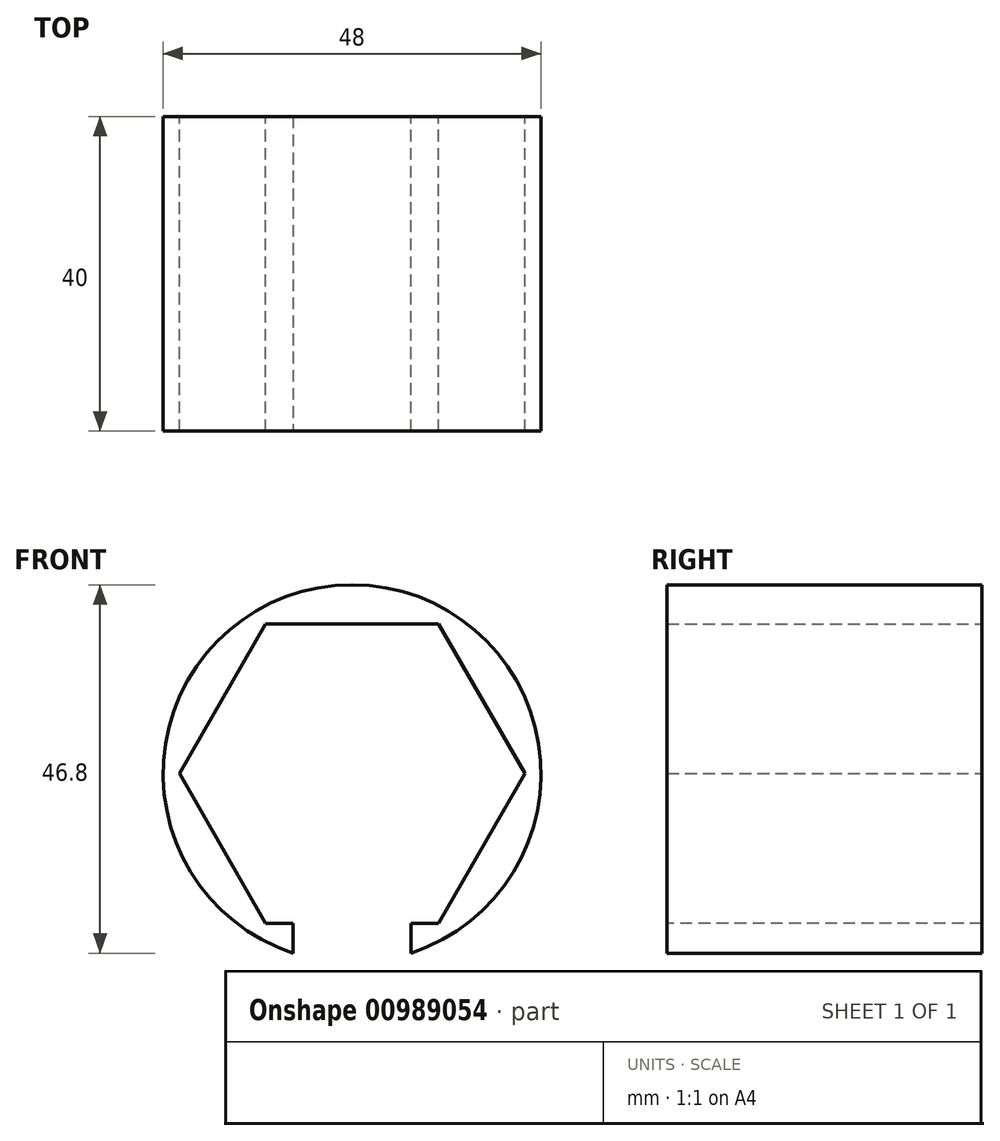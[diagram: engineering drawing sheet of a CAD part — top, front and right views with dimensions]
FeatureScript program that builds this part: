
annotation { "Feature Type Name" : "Feature", "Feature Type Description" : "" }
export const myFeature = defineFeature(function(context is Context, id is Id, definition is map)
    precondition{}
    {
        {
            var Q0;
            Q0=qCreatedBy(makeId("Front.planeOp"),FACE);
            var sketch = newSketch(context, id + "F0", { "sketchPlane" : qUnion([Q0])});
            skCircle(sketch, "E0.cCircle", {"center": v(0, 0) * mm, "radius": 19 * mm, "construction": true});
            skLineSegment(sketch, "E0.0", {"start": v(10.97, 19) * mm, "end": v(21.94, 0) * mm});
            skLineSegment(sketch, "E0.1", {"start": v(21.94, 0) * mm, "end": v(10.97, -19) * mm});
            skLineSegment(sketch, "E0.2", {"start": v(10.97, -19) * mm, "end": v(-10.97, -19) * mm});
            skLineSegment(sketch, "E0.3", {"start": v(-10.97, -19) * mm, "end": v(-21.94, 0) * mm});
            skLineSegment(sketch, "E0.4", {"start": v(-21.94, 0) * mm, "end": v(-10.97, 19) * mm});
            skLineSegment(sketch, "E0.5", {"start": v(-10.97, 19) * mm, "end": v(10.97, 19) * mm});
            skPoint(sketch, "E0.0.midPoint", {"position": v(16.45, 9.5) * mm});
            skCircle(sketch, "E1", {"center": v(0, 0) * mm, "radius": 24 * mm});
            skSolve(sketch);
        }
        {
            var Q0;
            Q0=makeQuery(id+"F0.imprint","IMPRINT",FACE,{"disambiguationData":[TD([[makeQuery(id+"F0.imprint","IMPRINT",EDGE,{"derivedFrom":sQuery(id+"F0.wireOp",EDGE,"E0.0")}),1.0]])]});
            extrude(context, id + "F1", {"entities" : qUnion([Q0]), "depth" : 40 * mm, "offsetDistance" : 25 * mm});
        }
        {
            var Q0;
            Q0=qCreatedBy(makeId("Top.planeOp"),FACE);
            var sketch = newSketch(context, id + "F2", { "sketchPlane" : qUnion([Q0])});
            skLineSegment(sketch, "E2.bottom", {"start": v(-7.5, -60) * mm, "end": v(7.5, -60) * mm});
            skLineSegment(sketch, "E2.top", {"start": v(-2.5, 10) * mm, "end": v(2.5, 10) * mm});
            skLineSegment(sketch, "E2.left", {"start": v(-7.5, -60) * mm, "end": v(-7.5, 5) * mm});
            skLineSegment(sketch, "E2.right", {"start": v(7.5, -60) * mm, "end": v(7.5, 5) * mm});
            skPoint(sketch, "E3.visualSharp", {"position": v(-7.5, 10) * mm});
            skArc(sketch, "E3.filletArc", {"start": v(-2.5, 10) * mm, "mid": v(-6.04, 8.54) * mm, "end": v(-7.5, 5) * mm});
            skPoint(sketch, "E4.visualSharp", {"position": v(7.5, 10) * mm});
            skArc(sketch, "E4.filletArc", {"start": v(7.5, 5) * mm, "mid": v(6.04, 8.54) * mm, "end": v(2.5, 10) * mm});
            skSolve(sketch);
        }
        {
            var Q0;
            Q0=makeQuery(id+"F2.imprint","IMPRINT",FACE,{"disambiguationData":[TD([[makeQuery(id+"F2.imprint","IMPRINT",EDGE,{"derivedFrom":sQuery(id+"F2.wireOp",EDGE,"E2.bottom")}),1.0]])]});
            extrude(context, id + "F3", {"entities" : qUnion([Q0]), "operationType" : NewBodyOperationType.REMOVE, "oppositeDirection" : true, "depth" : 100 * mm, "offsetDistance" : 25 * mm});
        }
    });
